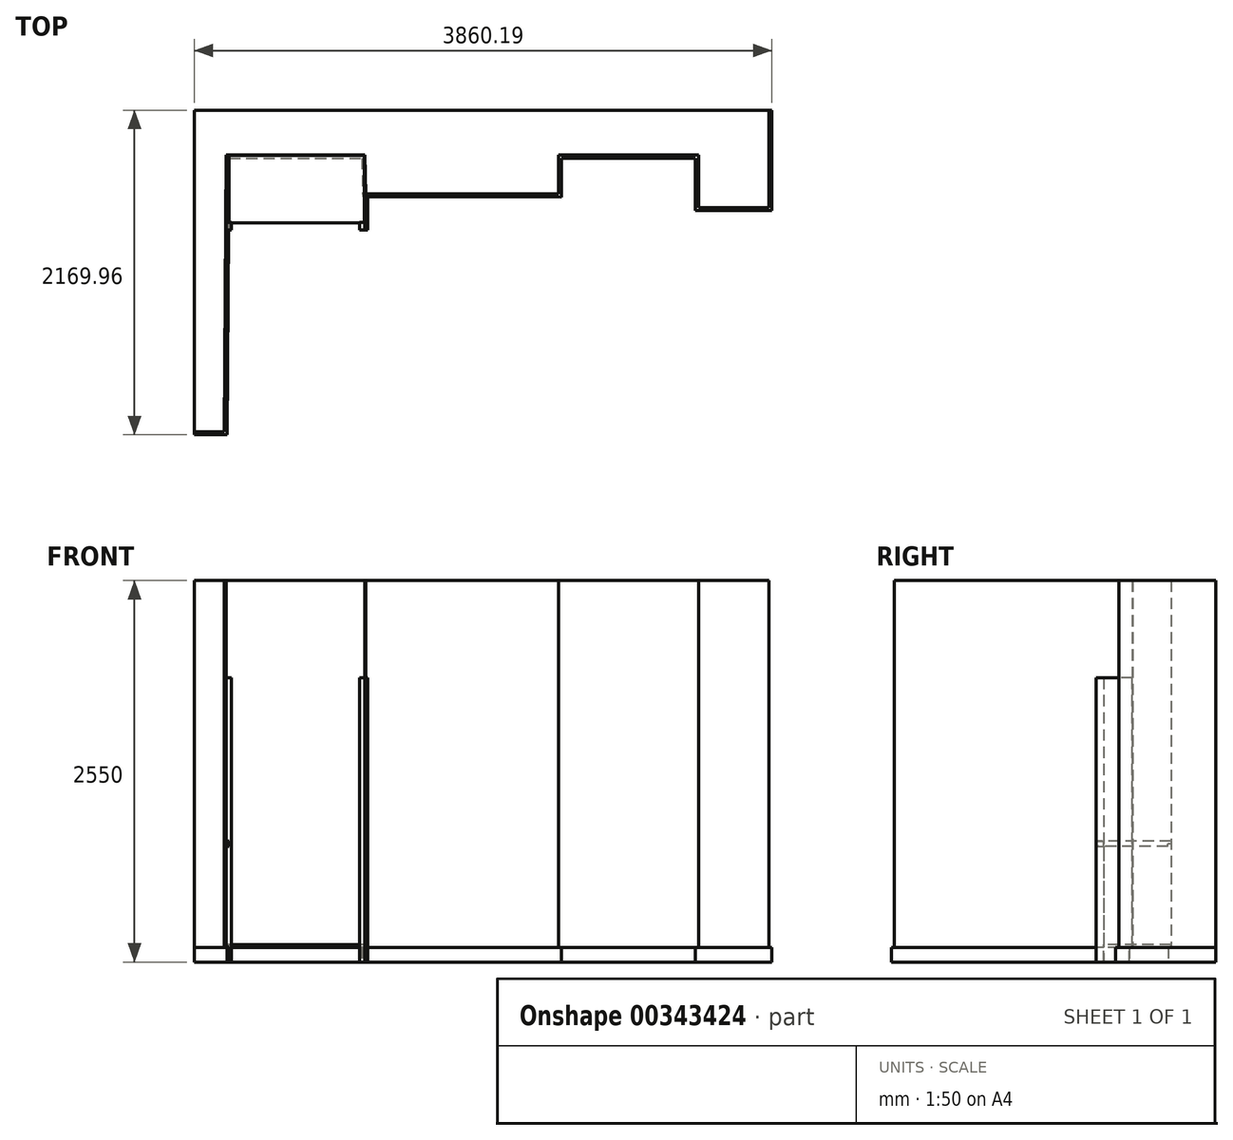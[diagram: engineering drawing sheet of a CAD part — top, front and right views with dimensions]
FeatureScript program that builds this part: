
annotation { "Feature Type Name" : "Feature", "Feature Type Description" : "" }
export const myFeature = defineFeature(function(context is Context, id is Id, definition is map)
    precondition{}
    {
        {
            var Q0;
            Q0=qCreatedBy(makeId("Top.planeOp"),FACE);
            var sketch = newSketch(context, id + "F0", { "sketchPlane" : qUnion([Q0])});
            skLineSegment(sketch, "E0", {"start": v(-11.82, -1849.96) * mm, "end": v(0, 0) * mm});
            skLineSegment(sketch, "E1", {"start": v(0, 0) * mm, "end": v(928, 0) * mm});
            skLineSegment(sketch, "E2", {"start": v(928, 0) * mm, "end": v(933.37, -257.94) * mm});
            skLineSegment(sketch, "E3", {"start": v(933.37, -257.94) * mm, "end": v(2223.37, -260) * mm});
            skLineSegment(sketch, "E4", {"start": v(2223.37, -260) * mm, "end": v(2223.37, 0) * mm});
            skLineSegment(sketch, "E5", {"start": v(2223.37, 0) * mm, "end": v(3158.37, 0) * mm});
            skLineSegment(sketch, "E6", {"start": v(3158.37, 0) * mm, "end": v(3158.37, -350) * mm});
            skLineSegment(sketch, "E7", {"start": v(3158.37, -350) * mm, "end": v(3628.37, -350) * mm});
            skLineSegment(sketch, "E8", {"start": v(-11.82, -1849.96) * mm, "end": v(-211.82, -1849.96) * mm});
            skLineSegment(sketch, "E9", {"start": v(-211.82, -1849.96) * mm, "end": v(-211.82, 300) * mm});
            skLineSegment(sketch, "E10", {"start": v(-211.82, 300) * mm, "end": v(3628.37, 300) * mm});
            skLineSegment(sketch, "E11", {"start": v(3628.37, 300) * mm, "end": v(3628.37, -350) * mm});
            skLineSegment(sketch, "E12.0", {"start": v(8.05, -1869.96) * mm, "end": v(-211.82, -1869.96) * mm});
            skLineSegment(sketch, "E12.1", {"start": v(8.05, -1869.96) * mm, "end": v(19.87, -20) * mm});
            skLineSegment(sketch, "E12.2", {"start": v(19.87, -20) * mm, "end": v(908.41, -20) * mm});
            skLineSegment(sketch, "E12.3", {"start": v(908.41, -20) * mm, "end": v(913.78, -277.91) * mm});
            skLineSegment(sketch, "E12.4", {"start": v(913.78, -277.91) * mm, "end": v(2243.37, -280.03) * mm});
            skLineSegment(sketch, "E12.5", {"start": v(2243.37, -280.03) * mm, "end": v(2243.37, -20) * mm});
            skLineSegment(sketch, "E12.6", {"start": v(3648.37, 300) * mm, "end": v(3648.37, -370) * mm});
            skLineSegment(sketch, "E12.7", {"start": v(3138.37, -370) * mm, "end": v(3648.37, -370) * mm});
            skLineSegment(sketch, "E12.8", {"start": v(3138.37, -20) * mm, "end": v(3138.37, -370) * mm});
            skLineSegment(sketch, "E12.9", {"start": v(2243.37, -20) * mm, "end": v(3138.37, -20) * mm});
            skLineSegment(sketch, "E13", {"start": v(-211.82, -1869.96) * mm, "end": v(-211.82, -1849.96) * mm});
            skLineSegment(sketch, "E14", {"start": v(3628.37, 300) * mm, "end": v(3648.37, 300) * mm});
            skSolve(sketch);
        }
        {
            var Q0;
            Q0=makeQuery(id+"F0.imprint","IMPRINT",FACE,{"disambiguationData":[TD([[makeQuery(id+"F0.imprint","IMPRINT",EDGE,{"derivedFrom":sQuery(id+"F0.wireOp",EDGE,"E0")}),1.0]])]});
            extrude(context, id + "F1", {"entities" : qUnion([Q0]), "depth" : 2550 * mm});
        }
        {
            var Q0;
            Q0=makeQuery(id+"F0.imprint","IMPRINT",FACE,{"disambiguationData":[TD([[makeQuery(id+"F0.imprint","IMPRINT",EDGE,{"derivedFrom":sQuery(id+"F0.wireOp",EDGE,"E0")}),-1.0]])]});
            extrude(context, id + "F2", {"entities" : qUnion([Q0]), "operationType" : NewBodyOperationType.ADD, "depth" : 98 * mm});
        }
        {
            var Q0;
            Q0=qCreatedBy(makeId("Top.planeOp"),FACE);
            var sketch = newSketch(context, id + "F3", { "sketchPlane" : qUnion([Q0])});
            skLineSegment(sketch, "E15.bottom", {"start": v(0, -500) * mm, "end": v(35, -500) * mm});
            skLineSegment(sketch, "E15.top", {"start": v(0, -450) * mm, "end": v(35, -450) * mm});
            skLineSegment(sketch, "E15.left", {"start": v(0, -500) * mm, "end": v(0, -450) * mm});
            skLineSegment(sketch, "E15.right", {"start": v(35, -500) * mm, "end": v(35, -450) * mm});
            skSolve(sketch);
        }
        {
            var Q0;
            Q0 = qSketchRegion(id + "F3", true);
            extrude(context, id + "F4", {"entities" : qUnion([Q0]), "depth" : 1900 * mm});
        }
        {
            var Q0;
            Q0=makeQuery(id+"F1.opExtrude","SWEPT_BODY",BODY,{"disambiguationData":[OSD([sQuery(id+"F0.wireOp",EDGE,"E0"),sQuery(id+"F0.wireOp",EDGE,"E1"),sQuery(id+"F0.wireOp",EDGE,"E2"),sQuery(id+"F0.wireOp",EDGE,"E3"),sQuery(id+"F0.wireOp",EDGE,"E4"),sQuery(id+"F0.wireOp",EDGE,"E5"),sQuery(id+"F0.wireOp",EDGE,"E6"),sQuery(id+"F0.wireOp",EDGE,"E7"),sQuery(id+"F0.wireOp",EDGE,"E8"),sQuery(id+"F0.wireOp",EDGE,"E9"),sQuery(id+"F0.wireOp",EDGE,"E10"),sQuery(id+"F0.wireOp",EDGE,"E11")])]});
            var Q1;
            Q1=makeQuery(id+"F4.opExtrude","SWEPT_BODY",BODY,{"disambiguationData":[OSD([sQuery(id+"F3.wireOp",EDGE,"E15.bottom"),sQuery(id+"F3.wireOp",EDGE,"E15.top"),sQuery(id+"F3.wireOp",EDGE,"E15.left"),sQuery(id+"F3.wireOp",EDGE,"E15.right")])]});
            booleanBodies(context, id + "F5", {"operationType" : BooleanOperationType.SUBTRACTION, "tools" : qUnion([Q0]), "targets" : qUnion([Q1]), "offset" : true, "offsetAll" : true, "offsetDistance" : 2 * mm, "keepTools" : true});
        }
        {
            var Q0;
            Q0=qCreatedBy(makeId("Top.planeOp"),FACE);
            var sketch = newSketch(context, id + "F6", { "sketchPlane" : qUnion([Q0])});
            skLineSegment(sketch, "E16.bottom", {"start": v(893, -500) * mm, "end": v(928, -500) * mm});
            skLineSegment(sketch, "E16.top", {"start": v(893, -450) * mm, "end": v(928, -450) * mm});
            skLineSegment(sketch, "E16.left", {"start": v(893, -500) * mm, "end": v(893, -450) * mm});
            skLineSegment(sketch, "E16.right", {"start": v(928, -500) * mm, "end": v(928, -450) * mm});
            skSolve(sketch);
        }
        {
            var Q0;
            Q0=makeQuery(id+"F6.imprint","IMPRINT",FACE,{"disambiguationData":[TD([[makeQuery(id+"F6.imprint","IMPRINT",EDGE,{"derivedFrom":sQuery(id+"F6.wireOp",EDGE,"u6PdSKaD-PTAn-jpHb-6gyG-SJ5LfTd6IVLw.bottom")}),1.0]])]});
            var Q1;
            Q1=makeQuery(id+"F6.imprint","IMPRINT",FACE,{"disambiguationData":[TD([[makeQuery(id+"F6.imprint","IMPRINT",EDGE,{"derivedFrom":sQuery(id+"F6.wireOp",EDGE,"E16.bottom")}),1.0]])]});
            var Q2;
            Q2=makeQuery(id+"F4.opExtrude","CAP_FACE",FACE,{"disambiguationData":[OSD([sQuery(id+"F3.wireOp",EDGE,"E15.bottom"),sQuery(id+"F3.wireOp",EDGE,"E15.top"),sQuery(id+"F3.wireOp",EDGE,"E15.left"),sQuery(id+"F3.wireOp",EDGE,"E15.right")])],"isStart":false});
            extrude(context, id + "F7", {"entities" : qUnion([Q0, Q1]), "endBound" : BoundingType.UP_TO_SURFACE, "endBoundEntityFace" : qUnion([Q2]), "depth" : 1500 * mm});
        }
        {
            assignVariable(context, id + "F8", {"name" : "shelf_thick", "anyValue" : 19});
        }
        {
            var Q0;
            Q0=makeQuery(id+"F2.opExtrude","CAP_FACE",FACE,{"disambiguationData":[OSD([sQuery(id+"F0.wireOp",EDGE,"E0"),sQuery(id+"F0.wireOp",EDGE,"E1"),sQuery(id+"F0.wireOp",EDGE,"E2"),sQuery(id+"F0.wireOp",EDGE,"E3"),sQuery(id+"F0.wireOp",EDGE,"E4"),sQuery(id+"F0.wireOp",EDGE,"E5"),sQuery(id+"F0.wireOp",EDGE,"E6"),sQuery(id+"F0.wireOp",EDGE,"E7"),sQuery(id+"F0.wireOp",EDGE,"E8"),sQuery(id+"F0.wireOp",EDGE,"E11"),sQuery(id+"F0.wireOp",EDGE,"E12.0"),sQuery(id+"F0.wireOp",EDGE,"E12.1"),sQuery(id+"F0.wireOp",EDGE,"E12.2"),sQuery(id+"F0.wireOp",EDGE,"E12.3"),sQuery(id+"F0.wireOp",EDGE,"E12.4"),sQuery(id+"F0.wireOp",EDGE,"E12.5"),sQuery(id+"F0.wireOp",EDGE,"E12.6"),sQuery(id+"F0.wireOp",EDGE,"E12.7"),sQuery(id+"F0.wireOp",EDGE,"E12.8"),sQuery(id+"F0.wireOp",EDGE,"E12.9"),sQuery(id+"F0.wireOp",EDGE,"E13"),sQuery(id+"F0.wireOp",EDGE,"E14")])],"isStart":false});
            var sketch = newSketch(context, id + "F9", { "sketchPlane" : qUnion([Q0])});
            skLineSegment(sketch, "E17", {"start": v(-0.89, -452) * mm, "end": v(1.99, -2) * mm});
            skLineSegment(sketch, "E18", {"start": v(1.99, -2) * mm, "end": v(926.04, -2) * mm});
            skLineSegment(sketch, "E19", {"start": v(926.04, -2) * mm, "end": v(926.04, -452) * mm});
            skLineSegment(sketch, "E20.trimOffspring", {"start": v(926.04, -452) * mm, "end": v(-0.89, -452) * mm});
            skSolve(sketch);
        }
        {
            var Q0;
            Q0 = qSketchRegion(id + "F9", true);
            extrude(context, id + "F10", {"entities" : qUnion([Q0]), "depth" : (getVariable(context, 'shelf_thick')) * mm});
        }
        {
            var Q0;
            Q0=makeQuery(id+"F4.opExtrude","SWEPT_FACE",FACE,{"disambiguationData":[OSD([sQuery(id+"F3.wireOp",EDGE,"E15.bottom")])]});
            var sketch = newSketch(context, id + "F11", { "sketchPlane" : qUnion([Q0])});
            skLineSegment(sketch, "E21.bottom", {"start": v(20, 773) * mm, "end": v(0, 773) * mm});
            skLineSegment(sketch, "E21.top", {"start": v(20, 808) * mm, "end": v(0, 808) * mm});
            skLineSegment(sketch, "E21.left", {"start": v(0, 808) * mm, "end": v(0, 773) * mm});
            skLineSegment(sketch, "E21.right", {"start": v(20, 808) * mm, "end": v(20, 773) * mm});
            skSolve(sketch);
        }
        {
            var Q0;
            Q0 = qSketchRegion(id + "F11", true);
            var Q1;
            Q1=makeQuery(id+"F1.opExtrude","SWEPT_FACE",FACE,{"disambiguationData":[OSD([sQuery(id+"F0.wireOp",EDGE,"E1")])]});
            extrude(context, id + "F12", {"entities" : qUnion([Q0]), "endBound" : BoundingType.UP_TO_SURFACE, "oppositeDirection" : true, "endBoundEntityFace" : qUnion([Q1]), "depth" : 25 * mm});
        }
        {
            var Q0;
            Q0=makeQuery(id+"F12.opExtrude","SWEPT_BODY",BODY,{"disambiguationData":[OSD([sQuery(id+"F11.wireOp",EDGE,"E21.bottom"),sQuery(id+"F11.wireOp",EDGE,"E21.top"),sQuery(id+"F11.wireOp",EDGE,"E21.left"),sQuery(id+"F11.wireOp",EDGE,"E21.right")])]});
            var Q1;
            Q1=makeQuery(id+"F4.opExtrude","SWEPT_BODY",BODY,{"disambiguationData":[OSD([sQuery(id+"F3.wireOp",EDGE,"E15.bottom"),sQuery(id+"F3.wireOp",EDGE,"E15.top"),sQuery(id+"F3.wireOp",EDGE,"E15.left"),sQuery(id+"F3.wireOp",EDGE,"E15.right")])]});
            booleanBodies(context, id + "F13", {"operationType" : BooleanOperationType.SUBTRACTION, "tools" : qUnion([Q0]), "targets" : qUnion([Q1]), "offset" : true, "offsetAll" : true, "offsetDistance" : 1 * mm, "keepTools" : true});
        }
        {
            var Q0;
            Q0=makeQuery(id+"F12.opExtrude","SWEPT_FACE",FACE,{"disambiguationData":[OSD([sQuery(id+"F11.wireOp",EDGE,"E21.right")])]});
            var sketch = newSketch(context, id + "F14", { "sketchPlane" : qUnion([Q0])});
            skLineSegment(sketch, "E22.bottom", {"start": v(0, 773) * mm, "end": v(-21, 773) * mm});
            skLineSegment(sketch, "E22.top", {"start": v(0, 790.5) * mm, "end": v(-21, 790.5) * mm});
            skLineSegment(sketch, "E22.left", {"start": v(0, 773) * mm, "end": v(0, 790.5) * mm});
            skLineSegment(sketch, "E22.right", {"start": v(-21, 773) * mm, "end": v(-21, 790.5) * mm});
            skLineSegment(sketch, "E23", {"start": v(-10.5, 790.5) * mm, "end": v(-10.5, 808) * mm, "construction": true});
            skSolve(sketch);
        }
        {
            var Q0;
            Q0 = qSketchRegion(id + "F14", true);
            var Q1;
            Q1=makeQuery(id+"F12.opExtrude","SWEPT_FACE",FACE,{"disambiguationData":[OSD([sQuery(id+"F11.wireOp",EDGE,"E21.left")])]});
            extrude(context, id + "F15", {"entities" : qUnion([Q0]), "operationType" : NewBodyOperationType.REMOVE, "endBound" : BoundingType.UP_TO_SURFACE, "oppositeDirection" : true, "endBoundEntityFace" : qUnion([Q1]), "depth" : 25 * mm});
        }
        {
            var Q0;
            Q0=makeQuery(id+"F7.opExtrude","SWEPT_FACE",FACE,{"disambiguationData":[OSD([sQuery(id+"F6.wireOp",EDGE,"E16.right")])]});
            var sketch = newSketch(context, id + "F16", { "sketchPlane" : qUnion([Q0])});
            skLineSegment(sketch, "E24", {"start": v(-500, 0) * mm, "end": v(-279.91, 0) * mm});
            skLineSegment(sketch, "E25", {"start": v(-279.91, 0) * mm, "end": v(-279.91, 100) * mm});
            skLineSegment(sketch, "E26", {"start": v(-279.91, 100) * mm, "end": v(-258.94, 100) * mm});
            skLineSegment(sketch, "E27", {"start": v(-258.94, 100) * mm, "end": v(-258.94, 1900) * mm});
            skLineSegment(sketch, "E28", {"start": v(-258.94, 1900) * mm, "end": v(-500, 1900) * mm});
            skLineSegment(sketch, "E29", {"start": v(-500, 1900) * mm, "end": v(-500, 0) * mm});
            skSolve(sketch);
        }
        {
            var Q0;
            Q0 = qSketchRegion(id + "F16", true);
            extrude(context, id + "F17", {"entities" : qUnion([Q0]), "depth" : (getVariable(context, 'shelf_thick')) * mm});
        }
    });
